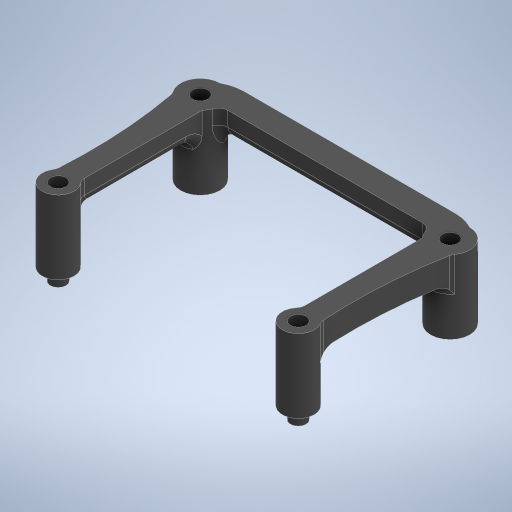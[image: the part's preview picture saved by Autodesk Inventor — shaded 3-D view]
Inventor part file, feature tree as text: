
AUTODESK INVENTOR PART (.ipt)
format: ipt  version: 2024.2 (Build 282272000, 272)  size: 482,304 bytes
history: native  units: mm
features: extrude x5, sketch x5, fillet x1, projected_geometry x1
ambient origin geometry x8: Origin, YZ Plane, XZ Plane, XY Plane, X Axis, Y Axis, Z Axis, Center Point
bodies: Solid1 (feature_tree)
feature tree (12):
  extrude  "Extrusion1"  Depth=5.0mm TaperAngle=0.0deg
  extrude  "Extrusion2"  Depth=5.2mm
  extrude  "Extrusion3"  Depth=8.0mm
  extrude  "Extrusion4"  Depth=49.0mm
  fillet  "Fillet1"  Radius=51.0mm
  extrude  "Extrusion5"  Depth=5.0mm
  sketch  "Sketch2"  dims[d0=6.5mm d1=5.0mm d2=0.0mm]
  sketch  "Sketch3"  dims[d3=6.5mm d4=5.2mm]
  sketch  "Sketch4"  dims[d5=5.2mm d6=8.0mm]
  projected_geometry  "Projected Loop1"
  sketch  "Sketch5"  dims[d7=8.0mm d8=49.0mm d9=51.0mm]
  sketch  "Sketch6"  dims[d11=30.0mm d12=3.2mm d13=3.2mm d14=2.5mm d15=0.0mm d16=3.0mm d17=3.0mm d18=5.0mm d19=0.0mm d21=1.0mm d24=100.0mm d25=100.0mm d26=2.5mm d27=3.0mm d28=3.0mm d29=2.5mm d30=5.0mm d31=0.0mm d32=5.0mm d33=4.0mm d34=4.0mm d35=2.0mm d36=5.0mm d37=0.0mm d38=3.2mm d39=3.2mm d40=3.0mm d41=3.0mm d20=0.5mm]
